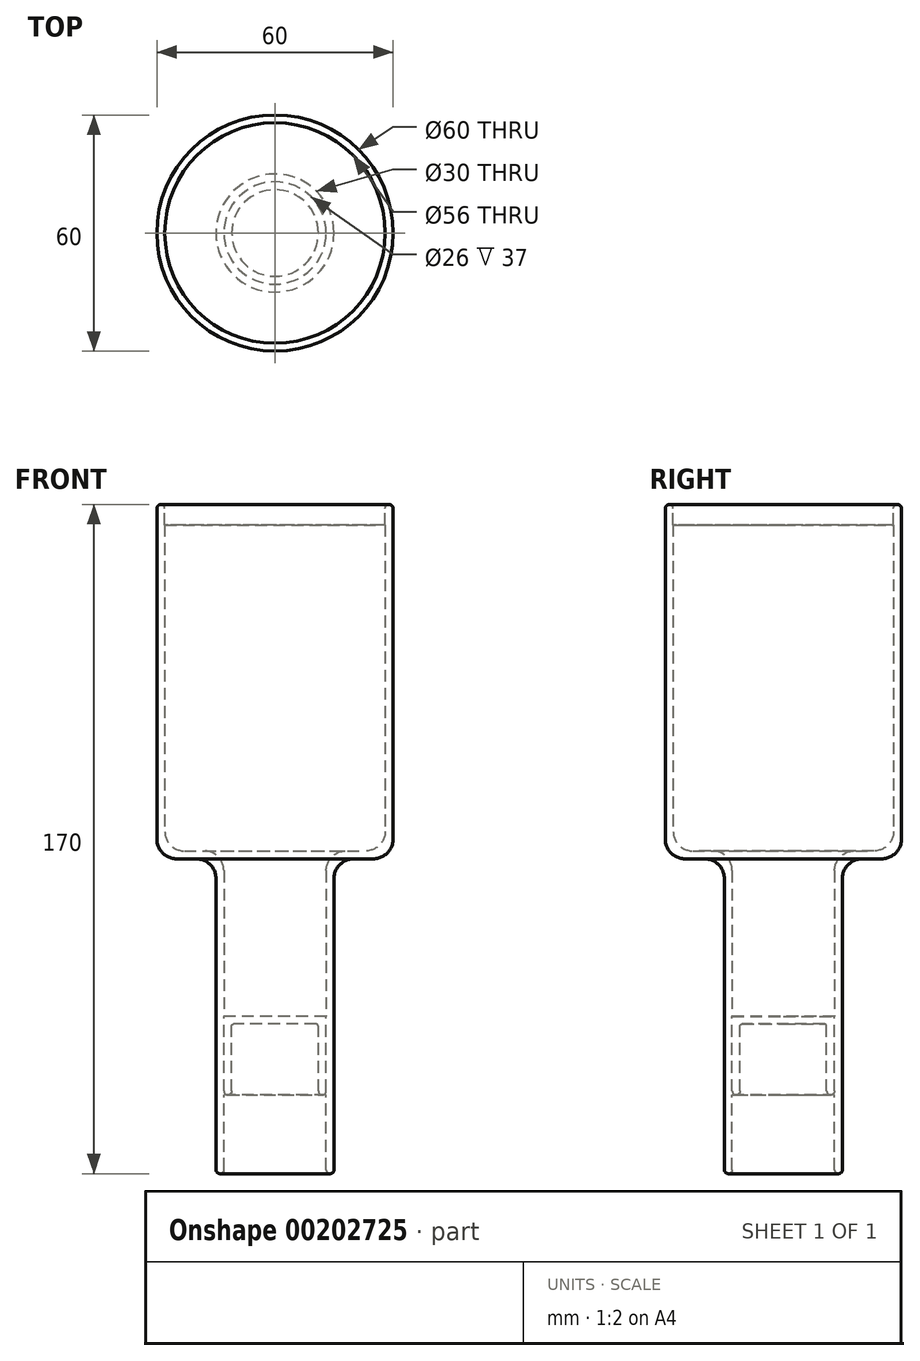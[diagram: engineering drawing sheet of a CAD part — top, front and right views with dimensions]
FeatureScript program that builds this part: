
annotation { "Feature Type Name" : "Feature", "Feature Type Description" : "" }
export const myFeature = defineFeature(function(context is Context, id is Id, definition is map)
    precondition{}
    {
        {
            var Q0;
            Q0=qCreatedBy(makeId("Front.planeOp"),FACE);
            var sketch = newSketch(context, id + "F0", { "sketchPlane" : qUnion([Q0])});
            skLineSegment(sketch, "E0", {"start": v(0, 0) * mm, "end": v(0, 90) * mm});
            skLineSegment(sketch, "E1", {"start": v(0, 90) * mm, "end": v(2, 90) * mm});
            skLineSegment(sketch, "E2", {"start": v(2, 90) * mm, "end": v(2, 84.81) * mm});
            skLineSegment(sketch, "E3", {"start": v(0, 0) * mm, "end": v(15, 0) * mm});
            skLineSegment(sketch, "E4", {"start": v(15, 0) * mm, "end": v(15, -80) * mm});
            skLineSegment(sketch, "E5", {"start": v(15, -80) * mm, "end": v(17, -80) * mm});
            skLineSegment(sketch, "E6", {"start": v(30, -80) * mm, "end": v(30, 56.65) * mm, "construction": true});
            skLineSegment(sketch, "E7.0", {"start": v(17, -60) * mm, "end": v(17, -80) * mm});
            skSolve(sketch);
        }
        {
            var Q0;
            Q0 = qSketchRegion(id + "F0", true);
            var Q1;
            Q1=sQuery(id+"F0.wireOp",EDGE,"E3");
            var Q2;
            Q2=sQuery(id+"F0.wireOp",EDGE,"E7.0");
            var Q3;
            Q3=sQuery(id+"F0.wireOp",EDGE,"E0");
            var Q4;
            Q4=sQuery(id+"F0.wireOp",EDGE,"E4");
            var Q5;
            Q5=sQuery(id+"F0.wireOp",EDGE,"E2");
            var Q6;
            Q6=sQuery(id+"F0.wireOp",EDGE,"E5");
            var Q7;
            Q7=sQuery(id+"F0.wireOp",EDGE,"E1");
            var Q8;
            Q8=sQuery(id+"F0.wireOp",EDGE,"E6");
            revolve(context, id + "F1", {"bodyType" : ToolBodyType.SURFACE, "entities" : qUnion([Q0]), "surfaceEntities" : qUnion([Q1, Q2, Q3, Q4, Q5, Q6, Q7]), "axis" : qUnion([Q8]), "revolveType" : RevolveType.FULL});
        }
        {
            var Q0;
            Q0=makeQuery(id+"F1.opRevolve","SWEPT_EDGE",EDGE,{"disambiguationData":[OSD([sQuery(id+"F0.wireOp",VERTEX,"E0.start")])]});
            var Q1;
            Q1=makeQuery(id+"F1.opRevolve","SWEPT_EDGE",EDGE,{"disambiguationData":[OSD([sQuery(id+"F0.wireOp",VERTEX,"E4.start")])]});
            fillet(context, id + "F2", {"entities" : qUnion([Q0, Q1]), "radius" : 5 * mm, "tangentPropagation" : true, "allowEdgeOverflow" : false});
        }
        {
            var Q0;
            Q0=makeQuery(id+"F1.opRevolve","SWEPT_FACE",FACE,{"disambiguationData":[OSD([sQuery(id+"F0.wireOp",EDGE,"E1")])]});
            var Q1;
            Q1=makeQuery(id+"F1.opRevolve","SWEPT_FACE",FACE,{"disambiguationData":[OSD([sQuery(id+"F0.wireOp",EDGE,"E5")])]});
            fillet(context, id + "F3", {"entities" : qUnion([Q0, Q1]), "radius" : 1 * mm, "tangentPropagation" : true, "allowEdgeOverflow" : false});
        }
        {
            var Q0;
            Q0=qCreatedBy(makeId("Front.planeOp"),FACE);
            var sketch = newSketch(context, id + "F4", { "sketchPlane" : qUnion([Q0])});
            skLineSegment(sketch, "E8.0", {"start": v(19, -60) * mm, "end": v(17, -60) * mm});
            skLineSegment(sketch, "E9.bottom", {"start": v(17, -60) * mm, "end": v(19, -60) * mm});
            skLineSegment(sketch, "E9.top", {"start": v(17, -40) * mm, "end": v(30, -40) * mm});
            skLineSegment(sketch, "E9.left", {"start": v(17, -60) * mm, "end": v(17, -40) * mm});
            skLineSegment(sketch, "E10.0", {"start": v(19, -60) * mm, "end": v(19, -42) * mm});
            skLineSegment(sketch, "E10.1", {"start": v(19, -42) * mm, "end": v(30, -42) * mm});
            skLineSegment(sketch, "E11", {"start": v(30, -60) * mm, "end": v(30, -40) * mm});
            skPoint(sketch, "E9.right.end.orphan", {"position": v(43, -40) * mm});
            skPoint(sketch, "E12.orphan", {"position": v(43, -60) * mm});
            skSolve(sketch);
        }
        {
            var Q0;
            Q0 = qSketchRegion(id + "F4", true);
            var Q1;
            Q1=sQuery(id+"F4.wireOp",EDGE,"E9.left");
            var Q2;
            Q2=sQuery(id+"F4.wireOp",EDGE,"E9.bottom");
            var Q3;
            Q3=sQuery(id+"F4.wireOp",EDGE,"E10.0");
            var Q4;
            Q4=sQuery(id+"F4.wireOp",EDGE,"E10.1");
            var Q5;
            Q5=sQuery(id+"F4.wireOp",EDGE,"E9.top");
            var Q6;
            Q6=sQuery(id+"F4.wireOp",EDGE,"E11");
            revolve(context, id + "F5", {"bodyType" : ToolBodyType.SURFACE, "entities" : qUnion([Q0]), "surfaceEntities" : qUnion([Q1, Q2, Q3, Q4, Q5]), "axis" : qUnion([Q6]), "revolveType" : RevolveType.FULL});
        }
        {
            var Q0;
            Q0=makeQuery(id+"F5.opRevolve","SWEPT_FACE",FACE,{"disambiguationData":[OSD([sQuery(id+"F4.wireOp",EDGE,"E9.bottom")])]});
            fillet(context, id + "F6", {"entities" : qUnion([Q0]), "radius" : 1 * mm, "tangentPropagation" : true, "allowEdgeOverflow" : false});
        }
        {
            var Q0;
            Q0=makeQuery(id+"F5.opRevolve","SWEPT_EDGE",EDGE,{"disambiguationData":[OSD([sQuery(id+"F4.wireOp",VERTEX,"E10.1.start")])]});
            fillet(context, id + "F7", {"entities" : qUnion([Q0]), "radius" : 0.5 * mm, "tangentPropagation" : true, "allowEdgeOverflow" : false});
        }
        {
            var Q0;
            Q0=qCreatedBy(makeId("Front.planeOp"),FACE);
            var sketch = newSketch(context, id + "F8", { "sketchPlane" : qUnion([Q0])});
            skLineSegment(sketch, "E13.0", {"start": v(17, -40) * mm, "end": v(30, -40) * mm});
            skLineSegment(sketch, "E14.0", {"start": v(30, 84.81) * mm, "end": v(58, 84.81) * mm});
            skPoint(sketch, "E15.orphan", {"position": v(0, 5) * mm});
            skLineSegment(sketch, "E16", {"start": v(30, 84.81) * mm, "end": v(30, 5) * mm, "construction": true});
            skPoint(sketch, "E17.orphan", {"position": v(60, 5) * mm});
            skLineSegment(sketch, "E18", {"start": v(2, 0) * mm, "end": v(30, 0) * mm});
            skLineSegment(sketch, "E19", {"start": v(30, 0) * mm, "end": v(30, 5) * mm});
            skLineSegment(sketch, "E20", {"start": v(2, 84.81) * mm, "end": v(2, 7) * mm});
            skLineSegment(sketch, "E21.0", {"start": v(7, 2) * mm, "end": v(12, 2) * mm});
            skArc(sketch, "E22.filletArc", {"start": v(2, 7) * mm, "mid": v(3.46, 3.46) * mm, "end": v(7, 2) * mm});
            skLineSegment(sketch, "E23", {"start": v(17, -40) * mm, "end": v(17, -3) * mm});
            skLineSegment(sketch, "E24.trimOffspring", {"start": v(2.42, 5) * mm, "end": v(2, 5) * mm});
            skPoint(sketch, "E25.visualSharp", {"position": v(17, 2) * mm});
            skArc(sketch, "E25.filletArc", {"start": v(17, -3) * mm, "mid": v(15.54, 0.54) * mm, "end": v(12, 2) * mm});
            skLineSegment(sketch, "E26", {"start": v(17, -40) * mm, "end": v(30, -40) * mm, "construction": true});
            skPoint(sketch, "E27.orphan", {"position": v(43, -40) * mm});
            skSolve(sketch);
        }
        {
            var Q0;
            Q0 = qSketchRegion(id + "F8", true);
            var Q1;
            Q1=sQuery(id+"F8.wireOp",EDGE,"E20");
            var Q2;
            Q2=sQuery(id+"F8.wireOp",EDGE,"E22.filletArc");
            var Q3;
            Q3=sQuery(id+"F8.wireOp",EDGE,"E21.0");
            var Q4;
            Q4=sQuery(id+"F8.wireOp",EDGE,"E25.filletArc");
            var Q5;
            Q5=sQuery(id+"F8.wireOp",EDGE,"E23");
            var Q6;
            Q6=sQuery(id+"F8.wireOp",EDGE,"E13.0");
            var Q7;
            Q7=sQuery(id+"F8.wireOp",EDGE,"E16");
            revolve(context, id + "F9", {"bodyType" : ToolBodyType.SURFACE, "entities" : qUnion([Q0]), "surfaceEntities" : qUnion([Q1, Q2, Q3, Q4, Q5, Q6]), "axis" : qUnion([Q7]), "revolveType" : RevolveType.FULL});
        }
        {
            var Q0;
            Q0=qCreatedBy(makeId("Front.planeOp"),FACE);
            var sketch = newSketch(context, id + "F10", { "sketchPlane" : qUnion([Q0])});
            skLineSegment(sketch, "E28.0", {"start": v(2, 84.81) * mm, "end": v(30, 84.81) * mm});
            skLineSegment(sketch, "E29", {"start": v(30, 84.81) * mm, "end": v(30, 76.81) * mm});
            skPoint(sketch, "E30.orphan", {"position": v(58, 84.81) * mm});
            skSolve(sketch);
        }
        {
            var Q0;
            Q0 = qSketchRegion(id + "F10", true);
            var Q1;
            Q1=sQuery(id+"F10.wireOp",EDGE,"E28.0");
            var Q2;
            Q2=sQuery(id+"F10.wireOp",EDGE,"E29");
            revolve(context, id + "F11", {"bodyType" : ToolBodyType.SURFACE, "entities" : qUnion([Q0]), "surfaceEntities" : qUnion([Q1]), "axis" : qUnion([Q2]), "revolveType" : RevolveType.FULL});
        }
    });
